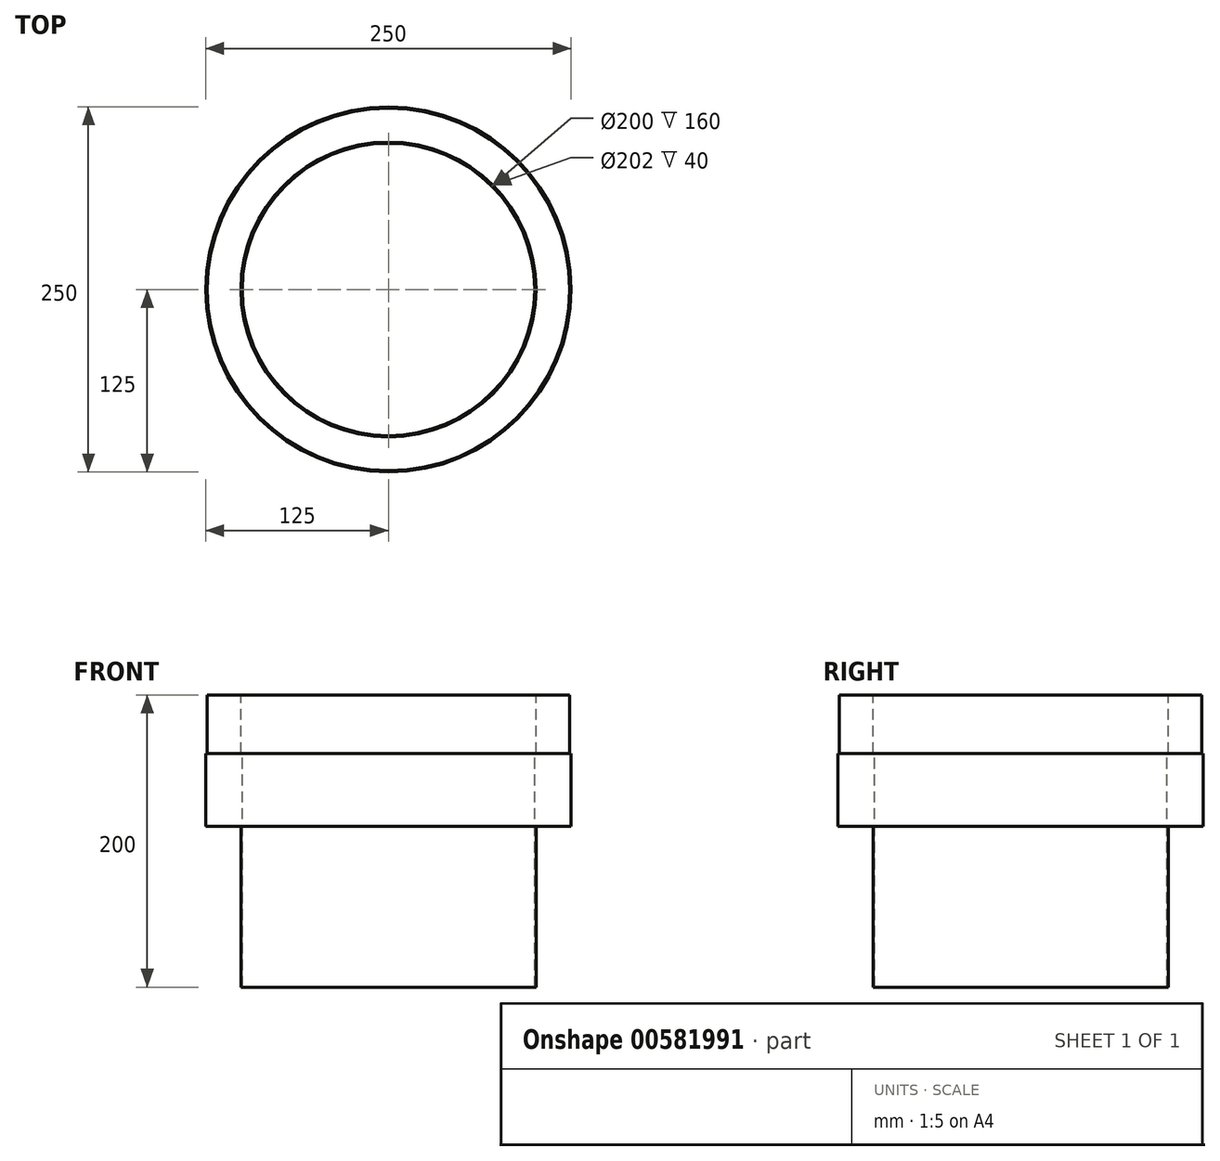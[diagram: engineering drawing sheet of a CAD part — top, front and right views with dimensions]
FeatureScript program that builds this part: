
annotation { "Feature Type Name" : "Feature", "Feature Type Description" : "" }
export const myFeature = defineFeature(function(context is Context, id is Id, definition is map)
    precondition{}
    {
        {
            var Q0;
            Q0=qCreatedBy(makeId("Front.planeOp"),FACE);
            var sketch = newSketch(context, id + "F0", { "sketchPlane" : qUnion([Q0])});
            skLineSegment(sketch, "E0", {"start": v(0, 710.75) * mm, "end": v(0, -704.58) * mm, "construction": true});
            skLineSegment(sketch, "E1", {"start": v(-100, 300.65) * mm, "end": v(-100, 410.65) * mm});
            skLineSegment(sketch, "E2", {"start": v(-100, 410.65) * mm, "end": v(-101, 410.65) * mm});
            skLineSegment(sketch, "E3", {"start": v(-124, 410.65) * mm, "end": v(-125, 410.65) * mm});
            skLineSegment(sketch, "E4", {"start": v(-125, 410.65) * mm, "end": v(-125, 360.65) * mm});
            skLineSegment(sketch, "E5", {"start": v(-125, 360.65) * mm, "end": v(-101, 360.65) * mm});
            skLineSegment(sketch, "E6", {"start": v(-101, 360.65) * mm, "end": v(-101, 300.65) * mm});
            skLineSegment(sketch, "E7", {"start": v(-124, 450.65) * mm, "end": v(-124, 410.65) * mm});
            skLineSegment(sketch, "E8", {"start": v(-124, 450.65) * mm, "end": v(-101, 450.65) * mm});
            skLineSegment(sketch, "E9", {"start": v(-101, 410.65) * mm, "end": v(-101, 450.65) * mm});
            skLineSegment(sketch, "E10", {"start": v(-100, 300.65) * mm, "end": v(-100, 250.65) * mm});
            skLineSegment(sketch, "E11", {"start": v(-101, 300.65) * mm, "end": v(-101, 250.65) * mm});
            skLineSegment(sketch, "E12", {"start": v(-101, 250.65) * mm, "end": v(-100, 250.65) * mm});
            skSolve(sketch);
        }
        {
            var Q0;
            Q0=qSketchRegion(id+"F0",true);
            var Q1;
            Q1=sQuery(id+"F0.wireOp",EDGE,"E0");
            revolve(context, id + "F1", {"entities" : qUnion([Q0]), "axis" : qUnion([Q1]), "revolveType" : RevolveType.FULL});
        }
    });
